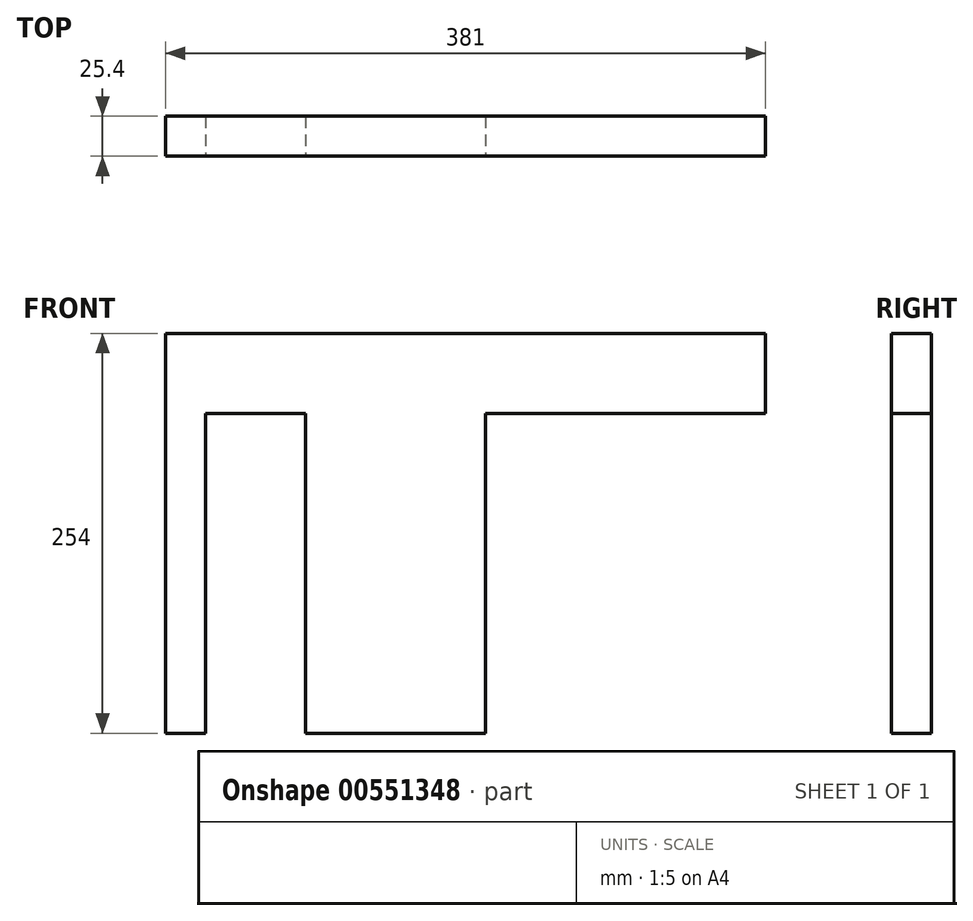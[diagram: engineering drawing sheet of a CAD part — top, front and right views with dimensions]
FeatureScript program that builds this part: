
annotation { "Feature Type Name" : "Feature", "Feature Type Description" : "" }
export const myFeature = defineFeature(function(context is Context, id is Id, definition is map)
    precondition{}
    {
        {
            var Q0;
            Q0=qCreatedBy(makeId("Front.planeOp"),FACE);
            var sketch = newSketch(context, id + "F0", { "sketchPlane" : qUnion([Q0])});
            skLineSegment(sketch, "E0.bottom", {"start": v(-311.63, 120.93) * mm, "end": v(69.37, 120.93) * mm});
            skLineSegment(sketch, "E0.top", {"start": v(-311.63, -133.07) * mm, "end": v(69.37, -133.07) * mm});
            skLineSegment(sketch, "E0.left", {"start": v(-311.63, 120.93) * mm, "end": v(-311.63, -133.07) * mm});
            skLineSegment(sketch, "E0.right", {"start": v(69.37, 120.93) * mm, "end": v(69.37, -133.07) * mm});
            skSolve(sketch);
        }
        {
            var Q0;
            Q0=makeQuery(id+"F0.imprint","IMPRINT",FACE,{"disambiguationData":[TD([[makeQuery(id+"F0.imprint","IMPRINT",EDGE,{"derivedFrom":sQuery(id+"F0.wireOp",EDGE,"E0.bottom")}),-1.0]])]});
            extrude(context, id + "F1", {"entities" : qUnion([Q0]), "depth" : 25.4 * mm, "offsetDistance" : 25.4 * mm});
        }
        {
            var Q0;
            Q0=makeQuery(id+"F1.opExtrude","CAP_FACE",FACE,{"disambiguationData":[OSD([sQuery(id+"F0.wireOp",EDGE,"E0.bottom"),sQuery(id+"F0.wireOp",EDGE,"E0.top"),sQuery(id+"F0.wireOp",EDGE,"E0.left"),sQuery(id+"F0.wireOp",EDGE,"E0.right")])],"isStart":false});
            var sketch = newSketch(context, id + "F2", { "sketchPlane" : qUnion([Q0])});
            skLineSegment(sketch, "E1.bottom", {"start": v(-286.23, 70.13) * mm, "end": v(-222.73, 70.13) * mm});
            skLineSegment(sketch, "E1.top", {"start": v(-286.23, -133.07) * mm, "end": v(-222.73, -133.07) * mm});
            skLineSegment(sketch, "E1.left", {"start": v(-286.23, 70.13) * mm, "end": v(-286.23, -133.07) * mm});
            skLineSegment(sketch, "E1.right", {"start": v(-222.73, 70.13) * mm, "end": v(-222.73, -133.07) * mm});
            skLineSegment(sketch, "E2.bottom", {"start": v(-108.43, 70.13) * mm, "end": v(69.37, 70.13) * mm});
            skLineSegment(sketch, "E2.top", {"start": v(-108.43, -133.07) * mm, "end": v(69.37, -133.07) * mm});
            skLineSegment(sketch, "E2.left", {"start": v(-108.43, 70.13) * mm, "end": v(-108.43, -133.07) * mm});
            skLineSegment(sketch, "E2.right", {"start": v(69.37, 70.13) * mm, "end": v(69.37, -133.07) * mm});
            skSolve(sketch);
        }
        {
            var Q0;
            Q0 = qSketchRegion(id + "F2", true);
            extrude(context, id + "F3", {"entities" : qUnion([Q0]), "operationType" : NewBodyOperationType.REMOVE, "oppositeDirection" : true, "depth" : 25.4 * mm, "offsetDistance" : 25.4 * mm});
        }
    });
